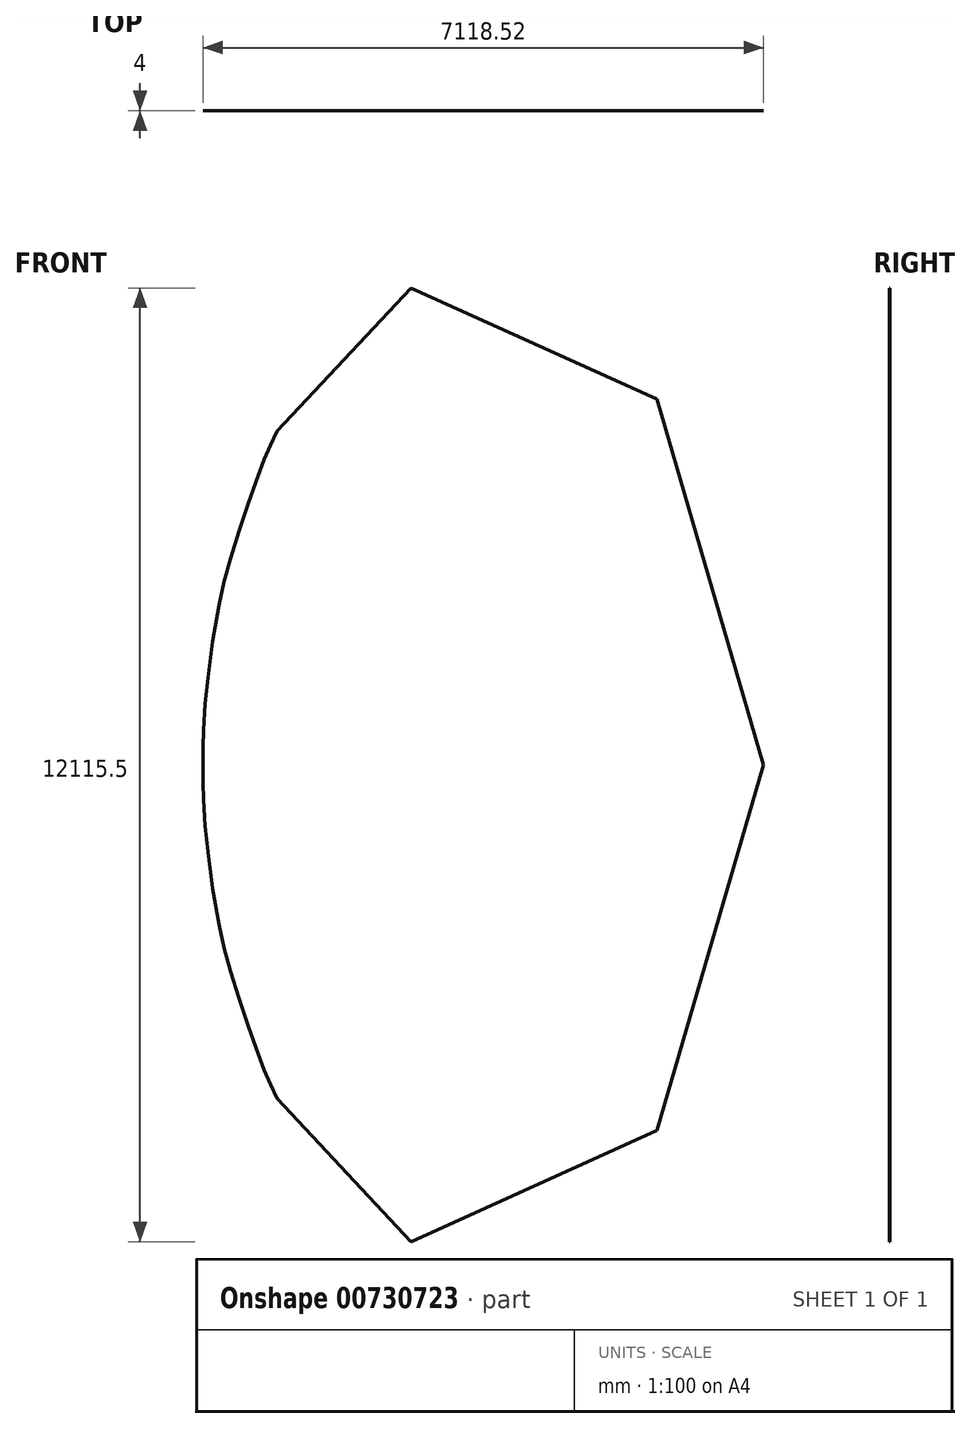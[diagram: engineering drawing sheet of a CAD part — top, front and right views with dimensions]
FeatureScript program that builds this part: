
annotation { "Feature Type Name" : "Feature", "Feature Type Description" : "" }
export const myFeature = defineFeature(function(context is Context, id is Id, definition is map)
    precondition{}
    {
        {
            var Q0;
            Q0=qCreatedBy(makeId("Front.planeOp"),FACE);
            var sketch = newSketch(context, id + "F0", { "sketchPlane" : qUnion([Q0])});
            skLineSegment(sketch, "E0", {"start": v(-919.62, -6057.73) * mm, "end": v(-2615.65, -4237.95) * mm});
            skLineSegment(sketch, "E1", {"start": v(-2615.65, -4237.95) * mm, "end": v(-2522.74, -4151.36) * mm});
            skLineSegment(sketch, "E2", {"start": v(-2522.74, -4151.36) * mm, "end": v(-2615.65, -4237.95) * mm});
            skLineSegment(sketch, "E3", {"start": v(-2615.65, -4237.95) * mm, "end": v(-2701.43, -4059.19) * mm});
            skLineSegment(sketch, "E4", {"start": v(-2701.43, -4059.19) * mm, "end": v(-2780.68, -3877.5) * mm});
            skLineSegment(sketch, "E5", {"start": v(-2780.68, -3877.5) * mm, "end": v(-2886.82, -3597.06) * mm});
            skLineSegment(sketch, "E6", {"start": v(-2886.82, -3597.06) * mm, "end": v(-2984.2, -3313.19) * mm});
            skLineSegment(sketch, "E7", {"start": v(-2984.2, -3313.19) * mm, "end": v(-3100.57, -2968.82) * mm});
            skLineSegment(sketch, "E8", {"start": v(-3100.57, -2968.82) * mm, "end": v(-3209.43, -2622.2) * mm});
            skLineSegment(sketch, "E9", {"start": v(-3209.43, -2622.2) * mm, "end": v(-3289.08, -2326.32) * mm});
            skLineSegment(sketch, "E10", {"start": v(-3289.08, -2326.32) * mm, "end": v(-3356.47, -2027.36) * mm});
            skLineSegment(sketch, "E11", {"start": v(-3356.47, -2027.36) * mm, "end": v(-3436.89, -1568.54) * mm});
            skLineSegment(sketch, "E12", {"start": v(-3436.89, -1568.54) * mm, "end": v(-3497.62, -1106.41) * mm});
            skLineSegment(sketch, "E13", {"start": v(-3497.62, -1106.41) * mm, "end": v(-3531.98, -775.3) * mm});
            skLineSegment(sketch, "E14", {"start": v(-3531.98, -775.3) * mm, "end": v(-3554.08, -443.37) * mm});
            skLineSegment(sketch, "E15", {"start": v(-3554.08, -443.37) * mm, "end": v(-3559.26, -221.7) * mm});
            skLineSegment(sketch, "E16", {"start": v(-3559.26, -221.7) * mm, "end": v(-3557.18, 0.01) * mm});
            skLineSegment(sketch, "E17", {"start": v(-3557.18, 0.01) * mm, "end": v(-3430.18, -1.18) * mm});
            skLineSegment(sketch, "E18", {"start": v(-3430.18, -1.18) * mm, "end": v(-3557.18, 0.01) * mm});
            skLineSegment(sketch, "E19", {"start": v(-3557.18, 0.01) * mm, "end": v(-3559.26, 221.73) * mm});
            skLineSegment(sketch, "E20", {"start": v(-3559.26, 221.73) * mm, "end": v(-3554.08, 443.37) * mm});
            skLineSegment(sketch, "E21", {"start": v(-3554.08, 443.37) * mm, "end": v(-3531.98, 775.32) * mm});
            skLineSegment(sketch, "E22", {"start": v(-3531.98, 775.32) * mm, "end": v(-3497.62, 1106.44) * mm});
            skLineSegment(sketch, "E23", {"start": v(-3497.62, 1106.44) * mm, "end": v(-3436.89, 1568.54) * mm});
            skLineSegment(sketch, "E24", {"start": v(-3436.89, 1568.54) * mm, "end": v(-3356.47, 2027.36) * mm});
            skLineSegment(sketch, "E25", {"start": v(-3356.47, 2027.36) * mm, "end": v(-3289.08, 2326.35) * mm});
            skLineSegment(sketch, "E26", {"start": v(-3289.08, 2326.35) * mm, "end": v(-3209.43, 2622.23) * mm});
            skLineSegment(sketch, "E27", {"start": v(-3209.43, 2622.23) * mm, "end": v(-3100.57, 2968.84) * mm});
            skLineSegment(sketch, "E28", {"start": v(-3100.57, 2968.84) * mm, "end": v(-2984.2, 3313.19) * mm});
            skLineSegment(sketch, "E29", {"start": v(-2984.2, 3313.19) * mm, "end": v(-2886.82, 3597.06) * mm});
            skLineSegment(sketch, "E30", {"start": v(-2886.82, 3597.06) * mm, "end": v(-2780.68, 3877.5) * mm});
            skLineSegment(sketch, "E31", {"start": v(-2780.68, 3877.5) * mm, "end": v(-2701.43, 4059.21) * mm});
            skLineSegment(sketch, "E32", {"start": v(-2701.43, 4059.21) * mm, "end": v(-2615.65, 4237.98) * mm});
            skLineSegment(sketch, "E33", {"start": v(-2615.65, 4237.98) * mm, "end": v(-2501.15, 4183.04) * mm});
            skLineSegment(sketch, "E34", {"start": v(-2501.15, 4183.04) * mm, "end": v(-2615.65, 4237.98) * mm});
            skLineSegment(sketch, "E35", {"start": v(-2615.65, 4237.98) * mm, "end": v(-919.62, 6057.73) * mm});
            skLineSegment(sketch, "E36", {"start": v(-919.62, 6057.73) * mm, "end": v(2204.43, 4647.22) * mm});
            skLineSegment(sketch, "E37", {"start": v(2204.43, 4647.22) * mm, "end": v(3559.26, 0.01) * mm});
            skLineSegment(sketch, "E38", {"start": v(3559.26, 0.01) * mm, "end": v(3437.34, -35.55) * mm});
            skLineSegment(sketch, "E39", {"start": v(3437.34, -35.55) * mm, "end": v(3559.26, 0.01) * mm});
            skLineSegment(sketch, "E40", {"start": v(3559.26, 0.01) * mm, "end": v(2204.43, -4647.2) * mm});
            skLineSegment(sketch, "E41", {"start": v(2204.43, -4647.2) * mm, "end": v(-919.62, -6057.73) * mm});
            skSolve(sketch);
        }
        {
            var Q0;
            Q0 = qSketchRegion(id + "F0", true);
            extrude(context, id + "F1", {"entities" : qUnion([Q0]), "depth" : 4 * mm, "offsetDistance" : 25 * mm});
        }
    });
